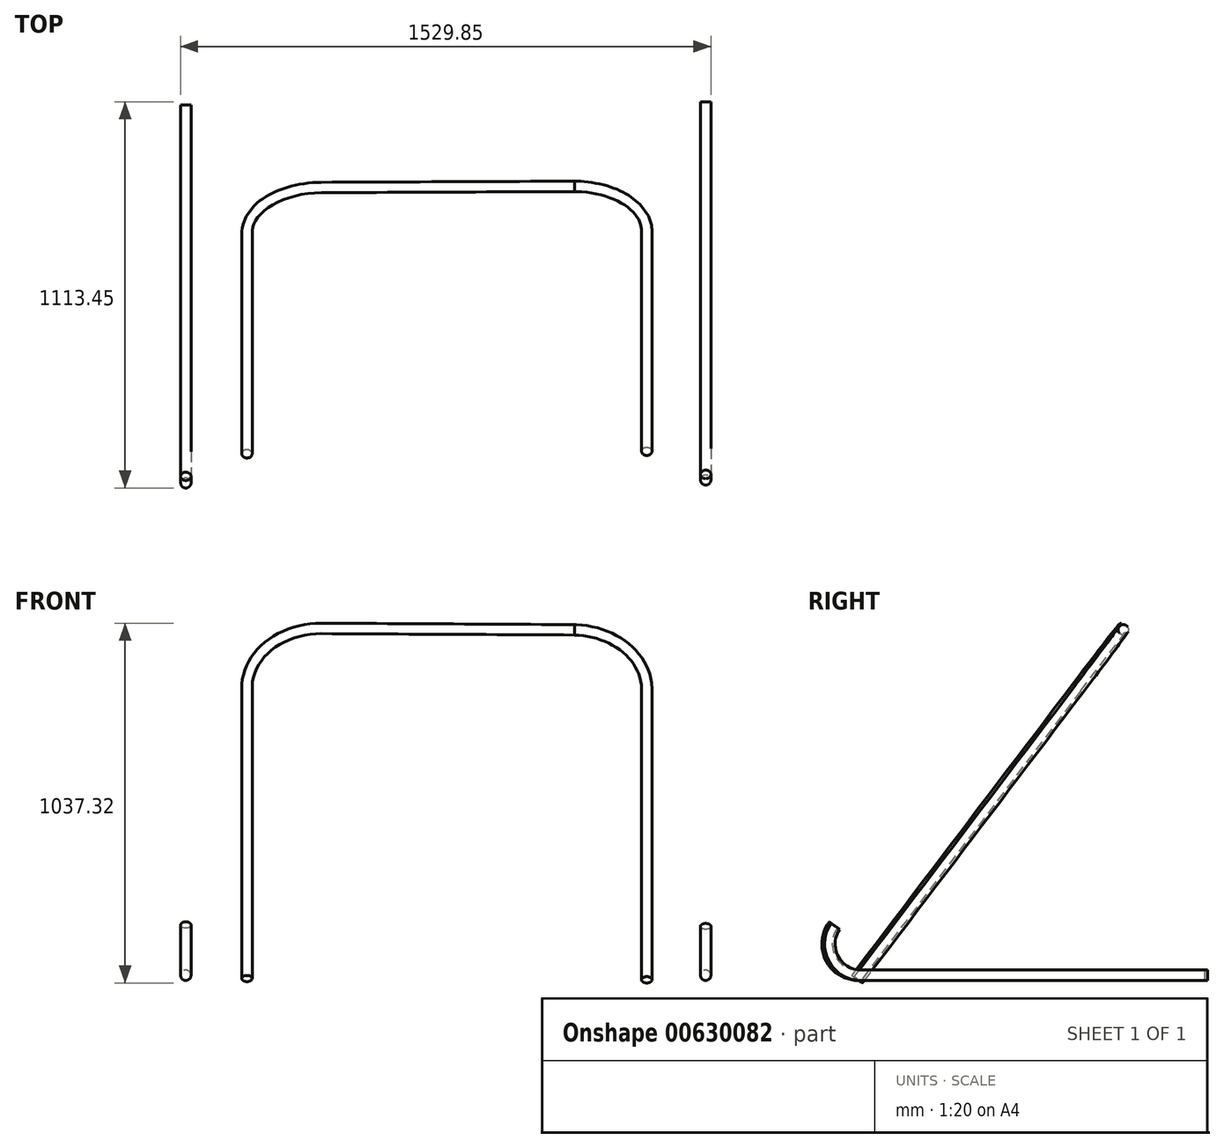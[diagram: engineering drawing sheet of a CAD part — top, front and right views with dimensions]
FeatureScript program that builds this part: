
annotation { "Feature Type Name" : "Feature", "Feature Type Description" : "" }
export const myFeature = defineFeature(function(context is Context, id is Id, definition is map)
    precondition{}
    {
        {
            var Q0;
            Q0=qCreatedBy(makeId("Front.planeOp"),FACE);
            var sketch = newSketch(context, id + "F0", { "sketchPlane" : qUnion([Q0])});
            skLineSegment(sketch, "E0", {"start": v(0, 1000) * mm, "end": v(500, 1000) * mm});
            skLineSegment(sketch, "E1", {"start": v(0, 1000) * mm, "end": v(-500, 1000) * mm});
            skSolve(sketch);
        }
        {
            var Q0;
            Q0=sQuery(id+"F0.wireOp",VERTEX,"E0.end");
            var Q1;
            Q1=qCreatedBy(makeId("Right.planeOp"),FACE);
            cPlane(context, id + "F1", {"entities" : qUnion([Q0, Q1]), "cplaneType" : CPlaneType.PLANE_POINT, "offset" : 25 * mm, "width" : 150 * mm, "height" : 150 * mm});
        }
        {
            var Q0;
            Q0=qCreatedBy(id+"F1.planeOp",FACE);
            var sketch = newSketch(context, id + "F2", { "sketchPlane" : qUnion([Q0])});
            skLineSegment(sketch, "E2", {"start": v(245.22, 0) * mm, "end": v(-754.78, 0) * mm});
            skArc(sketch, "E3", {"start": v(-754.78, 0) * mm, "mid": v(-834.44, 48.12) * mm, "end": v(-828.92, 141.03) * mm});
            skSolve(sketch);
        }
        {
            var Q0;
            Q0=qCreatedBy(makeId("Front.planeOp"),FACE);
            var sketch = newSketch(context, id + "F3", { "sketchPlane" : qUnion([Q0])});
            skCircle(sketch, "E4", {"center": v(750.03, 0) * mm, "radius": 15 * mm});
            skSolve(sketch);
        }
        {
            var Q0;
            Q0=sQuery(id+"F0.wireOp",VERTEX,"E1.end");
            var Q1;
            Q1=qCreatedBy(makeId("Right.planeOp"),FACE);
            cPlane(context, id + "F4", {"entities" : qUnion([Q0, Q1]), "cplaneType" : CPlaneType.PLANE_POINT, "offset" : 25 * mm, "width" : 150 * mm, "height" : 150 * mm});
        }
        {
            var Q0;
            Q0=qCreatedBy(id+"F4.planeOp",FACE);
            var sketch = newSketch(context, id + "F5", { "sketchPlane" : qUnion([Q0])});
            skLineSegment(sketch, "E5", {"start": v(236.77, 0) * mm, "end": v(-763.23, 0) * mm});
            skArc(sketch, "E6", {"start": v(-763.23, 0) * mm, "mid": v(-843.97, 50.24) * mm, "end": v(-834.57, 144.87) * mm});
            skSolve(sketch);
        }
        {
            var Q0;
            Q0=qCreatedBy(makeId("Front.planeOp"),FACE);
            var sketch = newSketch(context, id + "F6", { "sketchPlane" : qUnion([Q0])});
            skCircle(sketch, "E7", {"center": v(-749.82, 0) * mm, "radius": 15 * mm});
            skSolve(sketch);
        }
        {
            var Q0;
            Q0=sQuery(id+"F5.wireOp",VERTEX,"E6.end");
            var Q1;
            Q1=sQuery(id+"F2.wireOp",VERTEX,"E3.end");
            var Q2;
            Q2=sQuery(id+"F0.wireOp",VERTEX,"E1.start");
            cPlane(context, id + "F7", {"entities" : qUnion([Q0, Q1, Q2]), "cplaneType" : CPlaneType.THREE_POINT, "offset" : 25 * mm, "width" : 150 * mm, "height" : 150 * mm});
        }
        {
            var Q0;
            Q0=qCreatedBy(id+"F7.planeOp",FACE);
            var sketch = newSketch(context, id + "F8", { "sketchPlane" : qUnion([Q0])});
            skLineSegment(sketch, "E8", {"start": v(500.6, -472.8) * mm, "end": v(500.6, 580.14) * mm});
            skArc(sketch, "E9", {"start": v(500.6, 580.14) * mm, "mid": v(460.36, 677.78) * mm, "end": v(363.02, 718.72) * mm});
            skLineSegment(sketch, "E10", {"start": v(-499.05, -471.59) * mm, "end": v(-499.05, 580.14) * mm});
            skArc(sketch, "E11", {"start": v(-499.05, 580.14) * mm, "mid": v(-460.35, 675.76) * mm, "end": v(-366.03, 717.55) * mm});
            skLineSegment(sketch, "E12", {"start": v(363.02, 718.72) * mm, "end": v(-366.03, 717.55) * mm});
            skSolve(sketch);
        }
        {
            var Q0;
            Q0=qSketchRegion(id+"F3",true);
            var Q1;
            Q1=qConstructionFilter(qBodyType(qCreatedBy(id+"F2",EDGE),BodyType.WIRE),ConstructionObject.NO);
            sweep(context, id + "F9", {"profiles" : qUnion([Q0]), "path" : qUnion([Q1])});
        }
        {
            var Q0;
            Q0=qSketchRegion(id+"F6",true);
            var Q1;
            Q1=qConstructionFilter(qBodyType(qCreatedBy(id+"F5",EDGE),BodyType.WIRE),ConstructionObject.NO);
            sweep(context, id + "F10", {"profiles" : qUnion([Q0]), "path" : qUnion([Q1])});
        }
        {
            var Q0;
            Q0=qCreatedBy(makeId("Right.planeOp"),FACE);
            var sketch = newSketch(context, id + "F11", { "sketchPlane" : qUnion([Q0])});
            skCircle(sketch, "E13", {"center": v(0, 998.2) * mm, "radius": 15 * mm});
            skSolve(sketch);
        }
        {
            var Q0;
            Q0=qSketchRegion(id+"F11",true);
            var Q1;
            Q1=qConstructionFilter(qBodyType(qCreatedBy(id+"F8",EDGE),BodyType.WIRE),ConstructionObject.NO);
            sweep(context, id + "F12", {"profiles" : qUnion([Q0]), "path" : qUnion([Q1])});
        }
    });
